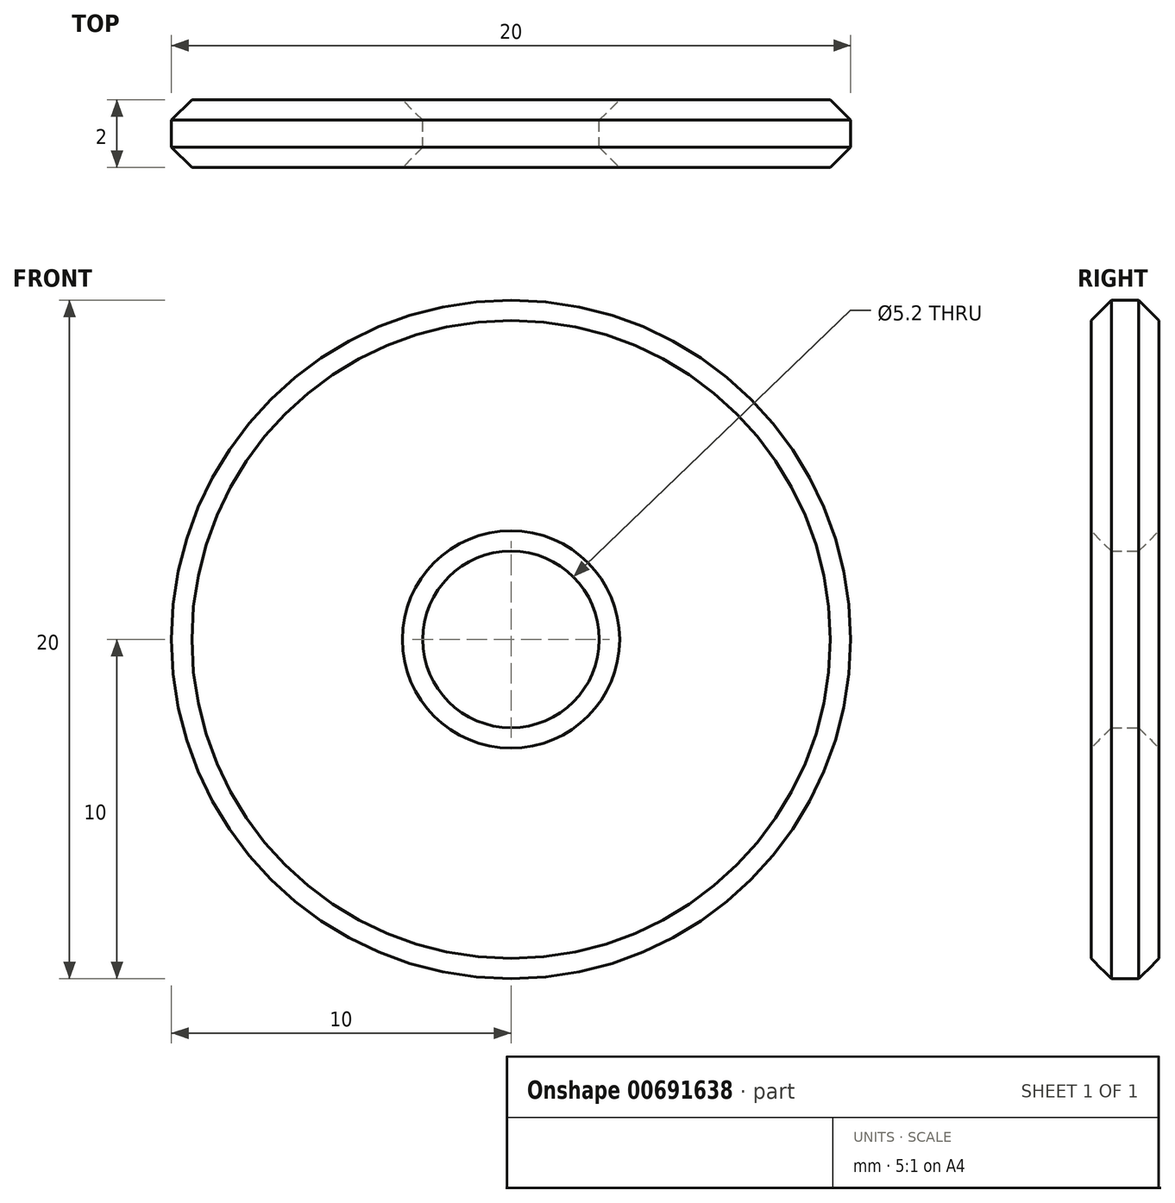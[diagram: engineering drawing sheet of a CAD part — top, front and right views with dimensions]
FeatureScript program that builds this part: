
annotation { "Feature Type Name" : "Feature", "Feature Type Description" : "" }
export const myFeature = defineFeature(function(context is Context, id is Id, definition is map)
    precondition{}
    {
        {
            var Q0;
            Q0=qCreatedBy(makeId("Front.planeOp"),FACE);
            var sketch = newSketch(context, id + "F0", { "sketchPlane" : qUnion([Q0])});
            skCircle(sketch, "E0", {"center": v(0, 0) * mm, "radius": 2.6 * mm});
            skCircle(sketch, "E1", {"center": v(0, 0) * mm, "radius": 10 * mm});
            skSolve(sketch);
        }
        {
            var Q0;
            Q0 = qSketchRegion(id + "F0", true);
            extrude(context, id + "F1", {"entities" : qUnion([Q0]), "depth" : 2 * mm, "offsetDistance" : 25 * mm});
        }
        {
            var Q0;
            Q0=makeQuery(id+"F1.opExtrude","CAP_FACE",FACE,{"disambiguationData":[OSD([sQuery(id+"F0.wireOp",EDGE,"E0"),sQuery(id+"F0.wireOp",EDGE,"E1")])],"isStart":false});
            var Q1;
            Q1=makeQuery(id+"F1.opExtrude","CAP_FACE",FACE,{"disambiguationData":[OSD([sQuery(id+"F0.wireOp",EDGE,"E0"),sQuery(id+"F0.wireOp",EDGE,"E1")])],"isStart":true});
            chamfer(context, id + "F2", {"entities" : qUnion([Q0, Q1]), "width" : .6 * mm, "tangentPropagation" : true});
        }
    });
